# Revit family: Seating_Ing-Grin_Round_Stool-1
name_source: partatom
category: Furniture
revit_build: Autodesk Revit 2014 (Build: 20130308_1515(x64)
units: mm (PartAtom-declared; Revit-internal decimal feet)

## types (3) — shared parameters
Aluminum Finish = STI - Aluminum
Arm Finish = STI - Plastic Black
Assembly Code = E2020200
Back Finish = STI - Plastic Black
Base Finish = STI - Plastic Black
Caster Finish = STI - Plastic Black
Depth = 25"
Front Finish = STI - Fabric Black
Hardware Finish = STI - Plastic Black
Height = 46"
Keynote = 12500
Low Emitting Finish = Yes
Low Emitting Material = Yes
Manufacturer = Seating Inc
Plastic Finish = STI - Plastic Black
Salvage or Reuse = Yes
Seat Finish = STI - Leather
Type Comments = Quick Configuration
URL = www.seatinginc.com
Width = 25"
zero-valued in all types: Percentage of Recycled Content

## per-type parameters (varying)
| type | Control 1 | Control 2 | Control 3 | Description | Seat Dist |
| Q-3GRST-A | Yes | No | No | Grid Round Mid Back Stool Basic Model 25W x 25D x 46H
Grid Round Mid Back Stool Basic Model 25W x 25D x 46H
Grid Round Mid Back Stool Basic Model 25W x 25D x 46H | 30 29/32" |
| Q-3GRST-B | No | Yes | No | Grid Round Mid Back Stool Value Packed 25W x 25D x 46H | 30 11/16" |
| Q-3GRST-C | No | No | Yes | Grid Round Mid Back Stool Fully Loaded 25W x 25D x 46H | 30 11/16" |

note: column(s) folded — value = type name in every type: Model

## geometry (parser evidence)
native form markers: Sweep x4
no freeform markers — native parametric forms only
